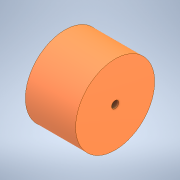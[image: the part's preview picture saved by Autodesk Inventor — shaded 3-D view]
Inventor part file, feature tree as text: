
AUTODESK INVENTOR PART (.ipt)
format: ipt  version: 2021 (Build 250183000, 183)  size: 98,816 bytes
history: imported  units: in
note: dims shown in document units (in); Inventor stores cm internally (conversion verified against a paired STEP export)
features: imported_body x1
ambient origin geometry x8: Origin, YZ Plane, XZ Plane, XY Plane, X Axis, Y Axis, Z Axis, Center Point
bodies: Solid1 (imported_parasolid), Body1 (imported_parasolid)
feature tree (1):
  imported_body  NMx_Import_Brep_tag  [imported B-rep: ~4 faces, bbox_mm=[21.0, 15.0, 0.0]]
